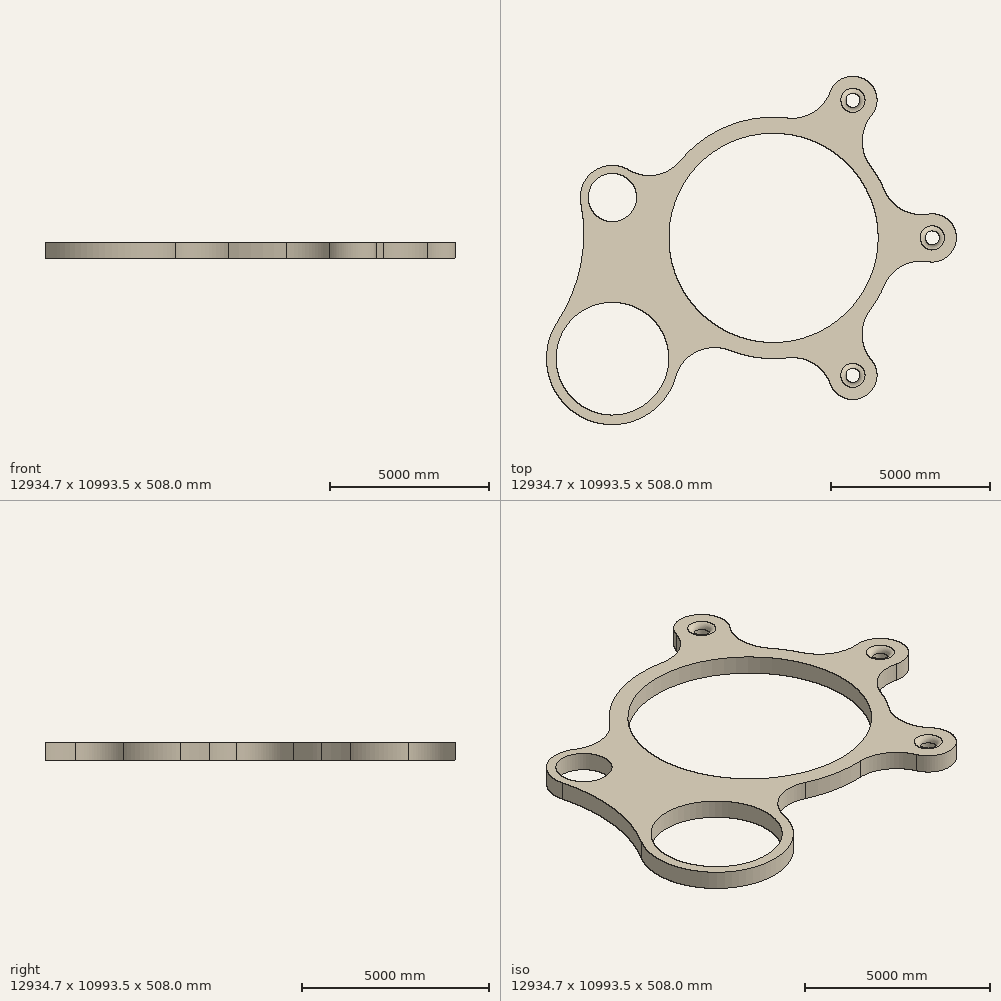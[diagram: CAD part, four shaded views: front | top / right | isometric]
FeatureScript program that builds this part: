
annotation { "Feature Type Name" : "Feature", "Feature Type Description" : "" }
export const myFeature = defineFeature(function(context is Context, id is Id, definition is map)
    precondition{}
    {
        {
            var Q0;
            Q0=qCreatedBy(makeId("Top.planeOp"),FACE);
            var sketch = newSketch(context, id + "F0", { "sketchPlane" : qUnion([Q0])});
            skCircle(sketch, "E0", {"center": v(0, 0) * mm, "radius": 3302 * mm});
            skPoint(sketch, "E1", {"position": v(-5080, -3810) * mm});
            skPoint(sketch, "E2", {"position": v(-5080, 1270) * mm});
            skCircle(sketch, "E3", {"center": v(-5080, -3810) * mm, "radius": 1778 * mm});
            skCircle(sketch, "E4", {"center": v(-5080, 1270) * mm, "radius": 762 * mm});
            skPoint(sketch, "E5", {"position": v(5009.9, 0) * mm});
            skCircle(sketch, "E6", {"center": v(5009.9, 0) * mm, "radius": 219.96 * mm});
            skLineSegment(sketch, "E7", {"start": v(0, 0) * mm, "end": v(1597.71, 0) * mm});
            skLineSegment(sketch, "E8", {"start": v(1120.83, 647.11) * mm, "end": v(0, 0) * mm});
            skCircle(sketch, "E9.MirrorC", {"center": v(2504.95, 4338.7) * mm, "radius": 219.96 * mm});
            skPoint(sketch, "E10.MirrorP", {"position": v(2504.95, -4338.7) * mm});
            skCircle(sketch, "E11.MirrorC", {"center": v(2504.95, -4338.7) * mm, "radius": 219.96 * mm});
            skArc(sketch, "E12", {"start": v(-2936.37, 2427.72) * mm, "mid": v(-1416.14, 3537.04) * mm, "end": v(449.6, 3783.38) * mm});
            skArc(sketch, "E13", {"start": v(449.6, 3783.38) * mm, "mid": v(1262.07, 3961.06) * mm, "end": v(1790.4, 4603.38) * mm});
            skArc(sketch, "E14", {"start": v(1790.4, 4603.38) * mm, "mid": v(2885.95, 4998.6) * mm, "end": v(3091.44, 3852.21) * mm});
            skArc(sketch, "E15", {"start": v(3091.44, 3852.21) * mm, "mid": v(2799.34, 3073.52) * mm, "end": v(3051.7, 2281.05) * mm});
            skArc(sketch, "E16", {"start": v(3051.7, 2281.05) * mm, "mid": v(3299.56, 1905) * mm, "end": v(3501.3, 1502.32) * mm});
            skArc(sketch, "E17", {"start": v(3501.3, 1502.32) * mm, "mid": v(4061.42, 887.54) * mm, "end": v(4881.84, 751.16) * mm});
            skArc(sketch, "E18", {"start": v(4881.84, 751.16) * mm, "mid": v(5771.9, 0) * mm, "end": v(4881.84, -751.16) * mm});
            skArc(sketch, "E19", {"start": v(4881.84, -751.16) * mm, "mid": v(4061.42, -887.54) * mm, "end": v(3501.3, -1502.32) * mm});
            skArc(sketch, "E20", {"start": v(3501.3, -1502.32) * mm, "mid": v(3298.76, -1906.37) * mm, "end": v(3049.8, -2283.6) * mm});
            skArc(sketch, "E21", {"start": v(3049.8, -2283.6) * mm, "mid": v(2796.4, -3044.8) * mm, "end": v(3049.8, -3805.99) * mm});
            skArc(sketch, "E22", {"start": v(-6077.83, 1078.7) * mm, "mid": v(-5664.34, 2101.14) * mm, "end": v(-4562.3, 2144.2) * mm});
            skArc(sketch, "E23", {"start": v(-3076.96, -4380.88) * mm, "mid": v(-5947.1, -5703.72) * mm, "end": v(-6820.89, -2666.6) * mm});
            skArc(sketch, "E24", {"start": v(-3076.96, -4380.88) * mm, "mid": v(-2418.97, -3590.76) * mm, "end": v(-1391.7, -3546.73) * mm});
            skArc(sketch, "E25", {"start": v(-1391.7, -3546.73) * mm, "mid": v(-485.68, -3778.92) * mm, "end": v(449.6, -3783.38) * mm});
            skArc(sketch, "E26", {"start": v(3049.8, -3805.99) * mm, "mid": v(2912.57, -4982.5) * mm, "end": v(1790.4, -4603.38) * mm});
            skArc(sketch, "E27", {"start": v(1790.4, -4603.38) * mm, "mid": v(1262.07, -3961.06) * mm, "end": v(449.6, -3783.38) * mm});
            skArc(sketch, "E28", {"start": v(-2936.37, 2427.72) * mm, "mid": v(-3697, 1985.84) * mm, "end": v(-4562.3, 2144.2) * mm});
            skArc(sketch, "E29", {"start": v(-6077.83, 1078.7) * mm, "mid": v(-6084.08, -866.42) * mm, "end": v(-6820.89, -2666.6) * mm});
            skSolve(sketch);
        }
        {
            var Q0;
            Q0 = qSketchRegion(id + "F0", true);
            extrude(context, id + "F1", {"entities" : qUnion([Q0]), "depth" : 508 * mm});
        }
        {
            var Q0;
            Q0=makeQuery(id+"F1.opExtrude","CAP_EDGE",EDGE,{"disambiguationData":[OSD([sQuery(id+"F0.wireOp",EDGE,"E11.MirrorC")])],"isStart":false});
            var Q1;
            Q1=makeQuery(id+"F1.opExtrude","CAP_EDGE",EDGE,{"disambiguationData":[OSD([sQuery(id+"F0.wireOp",EDGE,"E6")])],"isStart":false});
            var Q2;
            Q2=makeQuery(id+"F1.opExtrude","CAP_EDGE",EDGE,{"disambiguationData":[OSD([sQuery(id+"F0.wireOp",EDGE,"E9.MirrorC")])],"isStart":false});
            var Q3;
            Q3=makeQuery(id+"F1.opExtrude","CAP_EDGE",EDGE,{"disambiguationData":[OSD([sQuery(id+"F0.wireOp",EDGE,"E11.MirrorC")])],"isStart":true});
            var Q4;
            Q4=makeQuery(id+"F1.opExtrude","CAP_EDGE",EDGE,{"disambiguationData":[OSD([sQuery(id+"F0.wireOp",EDGE,"E6")])],"isStart":true});
            var Q5;
            Q5=makeQuery(id+"F1.opExtrude","CAP_EDGE",EDGE,{"disambiguationData":[OSD([sQuery(id+"F0.wireOp",EDGE,"E9.MirrorC")])],"isStart":true});
            fillet(context, id + "F2", {"entities" : qUnion([Q0, Q1, Q2, Q3, Q4, Q5]), "radius" : 161.04 * mm, "tangentPropagation" : true, "allowEdgeOverflow" : false});
        }
    });
